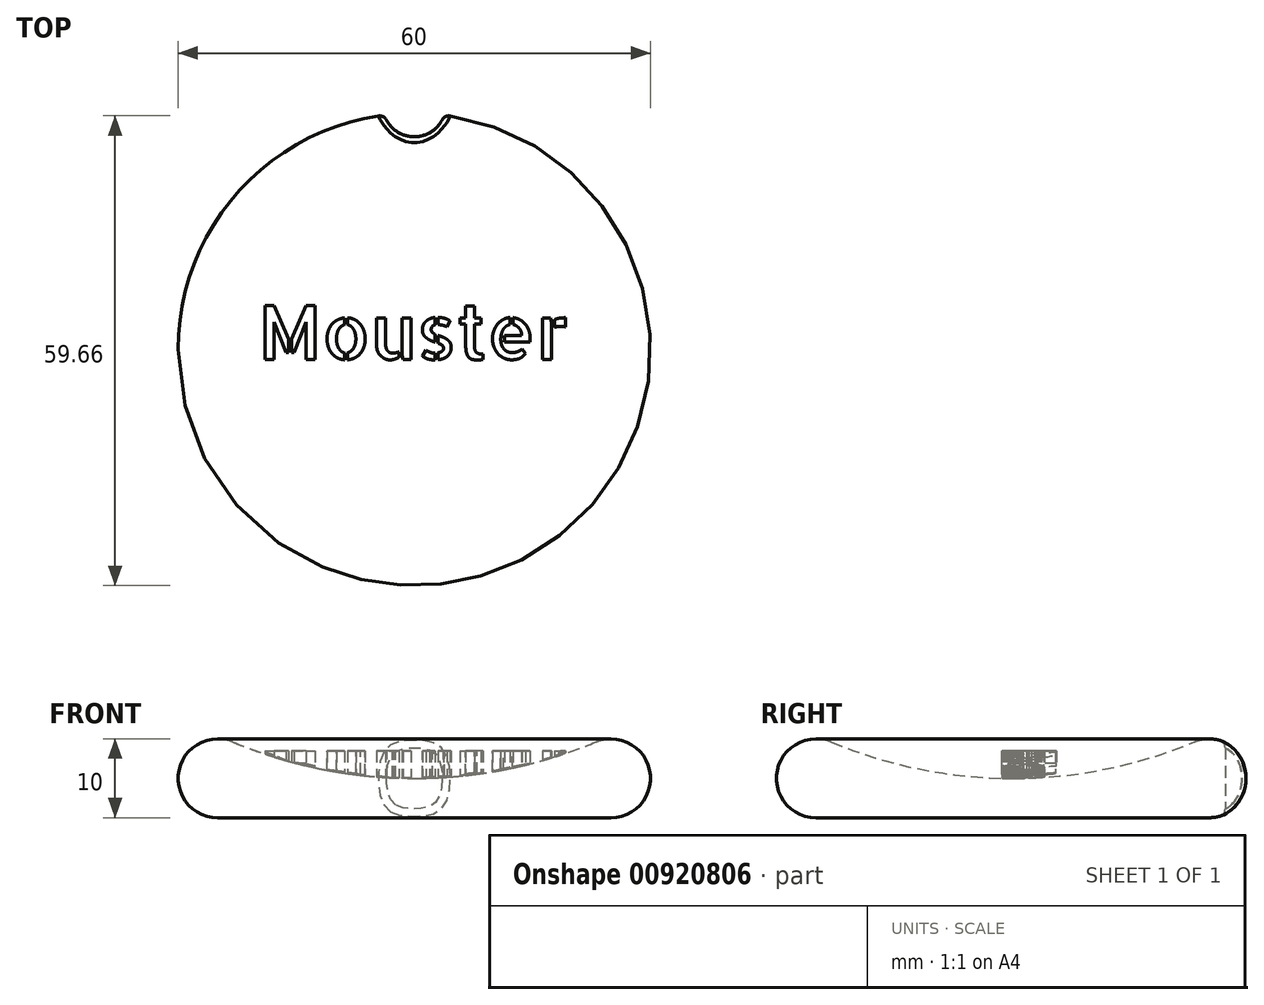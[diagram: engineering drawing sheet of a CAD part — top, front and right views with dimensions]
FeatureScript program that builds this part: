
annotation { "Feature Type Name" : "Feature", "Feature Type Description" : "" }
export const myFeature = defineFeature(function(context is Context, id is Id, definition is map)
    precondition{}
    {
        {
            var Q0;
            Q0=qCreatedBy(makeId("Front.planeOp"),FACE);
            var sketch = newSketch(context, id + "F0", { "sketchPlane" : qUnion([Q0])});
            skArc(sketch, "E0", {"start": v(-23.08, 9.62) * mm, "mid": v(-11.77, 6.17) * mm, "end": v(0, 5) * mm});
            skArc(sketch, "E1", {"start": v(-23.08, 9.62) * mm, "mid": v(-29.9, 5.98) * mm, "end": v(-25, 0) * mm});
            skLineSegment(sketch, "E2", {"start": v(-25, 0) * mm, "end": v(0, 0) * mm});
            skLineSegment(sketch, "E3", {"start": v(0, 0) * mm, "end": v(0, 5) * mm});
            skSolve(sketch);
        }
        {
            var Q0;
            Q0=makeQuery(id+"F0.imprint","IMPRINT",FACE,{"disambiguationData":[TD([[makeQuery(id+"F0.imprint","IMPRINT",EDGE,{"derivedFrom":sQuery(id+"F0.wireOp",EDGE,"E0")}),-1.0]])]});
            var Q1;
            Q1=sQuery(id+"F0.wireOp",EDGE,"E3");
            revolve(context, id + "F1", {"surfaceOperationType" : NewSurfaceOperationType.NEW, "entities" : qUnion([Q0]), "axis" : qUnion([Q1]), "revolveType" : RevolveType.FULL});
        }
        {
            var Q0;
            Q0=makeQuery(id+"F0.imprint","IMPRINT",FACE,{"disambiguationData":[TD([[makeQuery(id+"F0.imprint","IMPRINT",EDGE,{"derivedFrom":sQuery(id+"F0.wireOp",EDGE,"E0")}),-1.0]])]});
            var sketch = newSketch(context, id + "F2", { "sketchPlane" : qUnion([Q0])});
            skCircle(sketch, "E4", {"center": v(-25, 5) * mm, "radius": 4 * mm});
            skSolve(sketch);
        }
        {
            var Q0;
            Q0 = qSketchRegion(id + "F2", true);
            var Q1;
            Q1=sQuery(id+"F0.wireOp",EDGE,"E3");
            revolve(context, id + "F3", {"operationType" : NewBodyOperationType.ADD, "surfaceOperationType" : NewSurfaceOperationType.NEW, "entities" : qUnion([Q0]), "axis" : qUnion([Q1]), "revolveType" : RevolveType.FULL});
        }
        {
            var Q0;
            Q0=qCreatedBy(makeId("Top.planeOp"),FACE);
            var sketch = newSketch(context, id + "F4", { "sketchPlane" : qUnion([Q0])});
            skCircle(sketch, "E5", {"center": v(0, 31) * mm, "radius": 4 * mm});
            skSolve(sketch);
        }
        {
            var Q0;
            Q0=makeQuery(id+"F4.imprint","IMPRINT",FACE,{"disambiguationData":[TD([[makeQuery(id+"F4.imprint","IMPRINT",EDGE,{"derivedFrom":sQuery(id+"F4.wireOp",EDGE,"E5")}),1.0]])]});
            extrude(context, id + "F5", {"entities" : qUnion([Q0]), "operationType" : NewBodyOperationType.REMOVE, "depth" : 25 * mm, "offsetDistance" : 25 * mm});
        }
        {
            var Q0;
            Q0=makeQuery(id+"F5.boolean.opBoolean","INTERSECT",EDGE,{"derivedFrom":[makeQuery(id+"F1.opRevolve","SWEPT_FACE",FACE,{"disambiguationData":[OSD([sQuery(id+"F0.wireOp",EDGE,"E1")])]}),makeQuery(id+"F5.opExtrude","SWEPT_FACE",FACE,{"disambiguationData":[OSD([sQuery(id+"F4.wireOp",EDGE,"E5")])]})]});
            fillet(context, id + "F6", {"entities" : qUnion([Q0]), "radius" : 1 * mm, "tangentPropagation" : true, "allowEdgeOverflow" : false});
        }
        {
            var Q0;
            Q0=qCreatedBy(makeId("Top.planeOp"),FACE);
            var sketch = newSketch(context, id + "F7", { "sketchPlane" : qUnion([Q0])});
            skText(sketch, "E6", { "text": "Mouster", "fontName": "AllertaStencil-Regular.ttf"});
            const initialGuessF7  = {"E6": [-0.01984, -0.0013, 1, 0, 0.00689]};
            skSetInitialGuess(sketch, initialGuessF7);
            skSolve(sketch);
        }
        {
            var Q0;
            Q0 = qSketchRegion(id + "F7", true);
            extrude(context, id + "F8", {"entities" : qUnion([Q0]), "operationType" : NewBodyOperationType.ADD, "depth" : 8.5 * mm, "offsetDistance" : 25 * mm});
        }
    });
